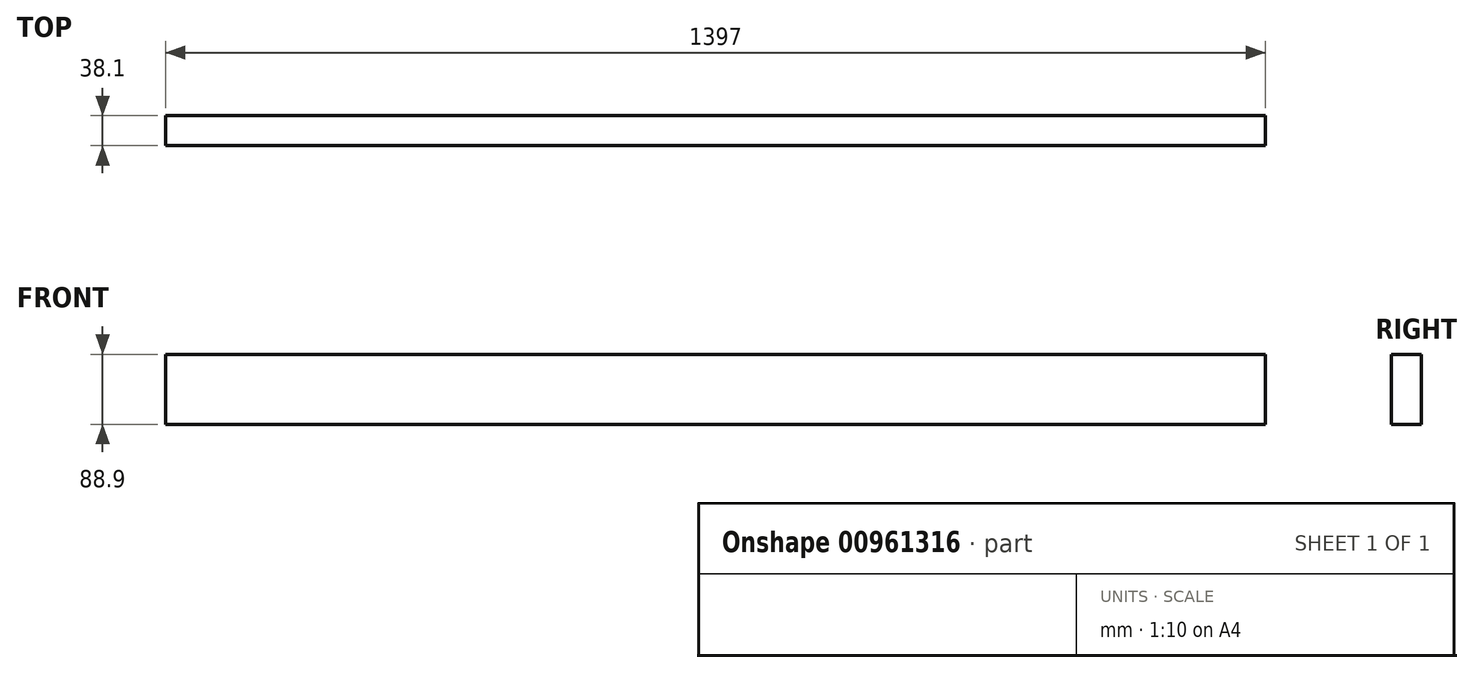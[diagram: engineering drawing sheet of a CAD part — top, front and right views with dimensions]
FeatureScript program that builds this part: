
annotation { "Feature Type Name" : "Feature", "Feature Type Description" : "" }
export const myFeature = defineFeature(function(context is Context, id is Id, definition is map)
    precondition{}
    {
        {
            var Q0;
            Q0=qCreatedBy(makeId("Right.planeOp"),FACE);
            var sketch = newSketch(context, id + "F0", { "sketchPlane" : qUnion([Q0])});
            skLineSegment(sketch, "E0.bottom", {"start": v(21, 44.45) * mm, "end": v(-17.1, 44.45) * mm});
            skLineSegment(sketch, "E0.top", {"start": v(21, -44.45) * mm, "end": v(-17.1, -44.45) * mm});
            skLineSegment(sketch, "E0.left", {"start": v(21, 44.45) * mm, "end": v(21, -44.45) * mm});
            skLineSegment(sketch, "E0.right", {"start": v(-17.1, 44.45) * mm, "end": v(-17.1, -44.45) * mm});
            skPoint(sketch, "E0.middle", {"position": v(1.94, 0) * mm});
            skSolve(sketch);
        }
        {
            var Q0;
            Q0=makeQuery(id+"F0.imprint","IMPRINT",FACE,{"disambiguationData":[TD([[makeQuery(id+"F0.imprint","IMPRINT",EDGE,{"derivedFrom":sQuery(id+"F0.wireOp",EDGE,"E0.bottom")}),1.0]])]});
            extrude(context, id + "F1", {"entities" : qUnion([Q0]), "endBound" : BoundingType.SYMMETRIC, "depth" : 1397 * mm, "offsetDistance" : 25.4 * mm});
        }
    });
